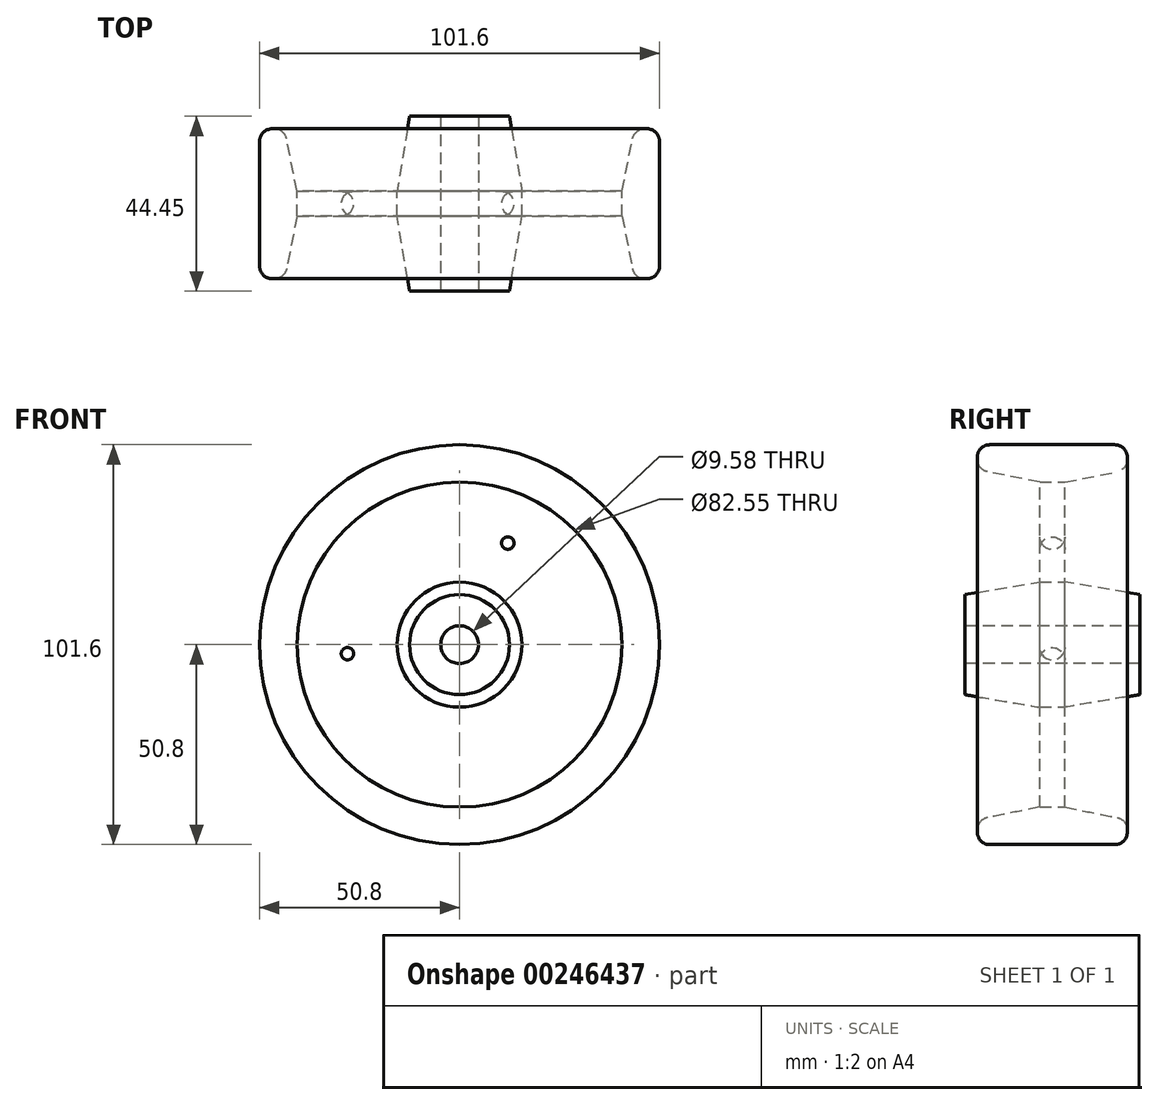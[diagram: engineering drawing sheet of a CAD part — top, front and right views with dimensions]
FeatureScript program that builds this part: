
annotation { "Feature Type Name" : "Feature", "Feature Type Description" : "" }
export const myFeature = defineFeature(function(context is Context, id is Id, definition is map)
    precondition{}
    {
        {
            var Q0;
            Q0=qCreatedBy(makeId("Right.planeOp"),FACE);
            var sketch = newSketch(context, id + "F0", { "sketchPlane" : qUnion([Q0])});
            skLineSegment(sketch, "E0", {"start": v(-6.26, 0) * mm, "end": v(19.14, 0) * mm});
            skLineSegment(sketch, "E1", {"start": v(-6.26, 4.79) * mm, "end": v(15.97, 4.79) * mm});
            skLineSegment(sketch, "E2", {"start": v(15.97, 4.79) * mm, "end": v(15.97, 50.8) * mm});
            skLineSegment(sketch, "E3", {"start": v(15.97, 50.8) * mm, "end": v(-3.08, 50.8) * mm});
            skLineSegment(sketch, "E4", {"start": v(-3.08, 50.8) * mm, "end": v(-3.08, 44.45) * mm});
            skLineSegment(sketch, "E5", {"start": v(-3.08, 44.45) * mm, "end": v(12.8, 41.28) * mm});
            skLineSegment(sketch, "E6", {"start": v(-6.26, 12.7) * mm, "end": v(12.8, 15.87) * mm});
            skLineSegment(sketch, "E7.trimOffspring", {"start": v(12.8, 15.87) * mm, "end": v(12.8, 41.28) * mm});
            skPoint(sketch, "E8.start.orphan", {"position": v(6.44, 0) * mm});
            skLineSegment(sketch, "E9.MirrorCS", {"start": v(35.02, 50.8) * mm, "end": v(35.02, 44.45) * mm});
            skLineSegment(sketch, "E10.MirrorCS", {"start": v(15.97, 50.8) * mm, "end": v(35.02, 50.8) * mm});
            skLineSegment(sketch, "E11.MirrorCS", {"start": v(35.02, 44.45) * mm, "end": v(19.14, 41.28) * mm});
            skLineSegment(sketch, "E12.MirrorCS", {"start": v(19.14, 15.88) * mm, "end": v(19.14, 41.28) * mm});
            skLineSegment(sketch, "E13.MirrorCS", {"start": v(38.2, 12.7) * mm, "end": v(19.14, 15.88) * mm});
            skLineSegment(sketch, "E14.MirrorCS", {"start": v(38.2, 0) * mm, "end": v(38.2, 12.7) * mm});
            skLineSegment(sketch, "E15.MirrorCS", {"start": v(38.2, 4.79) * mm, "end": v(15.97, 4.79) * mm});
            skLineSegment(sketch, "E16", {"start": v(-6.26, 12.7) * mm, "end": v(-6.26, 4.79) * mm});
            skSolve(sketch);
        }
        {
            var Q0;
            Q0=makeQuery(id+"F0.imprint","IMPRINT",FACE,{"disambiguationData":[TD([[makeQuery(id+"F0.imprint","IMPRINT",EDGE,{"derivedFrom":sQuery(id+"F0.wireOp",EDGE,"E2")}),-1.0]])]});
            var Q1;
            Q1=makeQuery(id+"F0.imprint","IMPRINT",FACE,{"disambiguationData":[TD([[makeQuery(id+"F0.imprint","IMPRINT",EDGE,{"derivedFrom":sQuery(id+"F0.wireOp",EDGE,"E1")}),1.0]])]});
            var Q2;
            Q2=sQuery(id+"F0.wireOp",EDGE,"E0");
            revolve(context, id + "F1", {"entities" : qUnion([Q0, Q1]), "axis" : qUnion([Q2]), "revolveType" : RevolveType.FULL});
        }
        {
            var Q0;
            Q0=makeQuery(id+"F1.opRevolve","SWEPT_FACE",FACE,{"disambiguationData":[OSD([sQuery(id+"F0.wireOp",EDGE,"E12.MirrorCS")])]});
            var sketch = newSketch(context, id + "F2", { "sketchPlane" : qUnion([Q0])});
            skCircle(sketch, "E17", {"center": v(0, 0) * mm, "radius": 28.58 * mm});
            skCircle(sketch, "E18", {"center": v(-12.26, 25.81) * mm, "radius": 4.76 * mm});
            skCircle(sketch, "E19.1.0", {"center": v(-16.23, -23.52) * mm, "radius": 4.76 * mm});
            skCircle(sketch, "E19.2.0", {"center": v(28.48, -2.3) * mm, "radius": 4.76 * mm});
            skSolve(sketch);
        }
        {
            var Q0;
            {var subQ0=sQuery(id+"F2.wireOp",EDGE,"E18");var subQ1=sQuery(id+"F2.wireOp",EDGE,"E17");var subQ2=makeQuery(id+"F2.imprint","INTERSECT",VERTEX,{"disambiguationData":[OD(0.0)],"derivedFrom":[subQ1,subQ0]});Q0=makeQuery(id+"F2.imprint","IMPRINT",FACE,{"disambiguationData":[TD([[makeQuery(id+"F2.imprint","IMPRINT",EDGE,{"disambiguationData":[TD([[subQ2,-1.0]])],"derivedFrom":subQ1}),1.0]])]});}
            var Q1;
            {var subQ0=sQuery(id+"F2.wireOp",EDGE,"E18");var subQ1=sQuery(id+"F2.wireOp",EDGE,"E17");var subQ2=makeQuery(id+"F2.imprint","INTERSECT",VERTEX,{"disambiguationData":[OD(0.0)],"derivedFrom":[subQ1,subQ0]});Q1=makeQuery(id+"F2.imprint","IMPRINT",FACE,{"disambiguationData":[TD([[makeQuery(id+"F2.imprint","IMPRINT",EDGE,{"disambiguationData":[TD([[subQ2,-1.0]])],"derivedFrom":subQ1}),-1.0]])]});}
            var Q2;
            {var subQ0=sQuery(id+"F2.wireOp",EDGE,"E19.2.0");var subQ1=sQuery(id+"F2.wireOp",EDGE,"E17");var subQ2=makeQuery(id+"F2.imprint","INTERSECT",VERTEX,{"disambiguationData":[OD(0.0)],"derivedFrom":[subQ1,subQ0]});Q2=makeQuery(id+"F2.imprint","IMPRINT",FACE,{"disambiguationData":[TD([[makeQuery(id+"F2.imprint","IMPRINT",EDGE,{"disambiguationData":[TD([[subQ2,1.0]])],"derivedFrom":subQ1}),1.0]])]});}
            var Q3;
            {var subQ0=sQuery(id+"F2.wireOp",EDGE,"E19.2.0");var subQ1=sQuery(id+"F2.wireOp",EDGE,"E17");var subQ2=makeQuery(id+"F2.imprint","INTERSECT",VERTEX,{"disambiguationData":[OD(0.0)],"derivedFrom":[subQ1,subQ0]});Q3=makeQuery(id+"F2.imprint","IMPRINT",FACE,{"disambiguationData":[TD([[makeQuery(id+"F2.imprint","IMPRINT",EDGE,{"disambiguationData":[TD([[subQ2,1.0]])],"derivedFrom":subQ1}),-1.0]])]});}
            var Q4;
            {var subQ0=sQuery(id+"F2.wireOp",EDGE,"E19.1.0");var subQ1=sQuery(id+"F2.wireOp",EDGE,"E17");var subQ2=makeQuery(id+"F2.imprint","INTERSECT",VERTEX,{"disambiguationData":[OD(0.0)],"derivedFrom":[subQ1,subQ0]});Q4=makeQuery(id+"F2.imprint","IMPRINT",FACE,{"disambiguationData":[TD([[makeQuery(id+"F2.imprint","IMPRINT",EDGE,{"disambiguationData":[TD([[subQ2,-1.0]])],"derivedFrom":subQ1}),-1.0]])]});}
            var Q5;
            {var subQ0=sQuery(id+"F2.wireOp",EDGE,"E19.1.0");var subQ1=sQuery(id+"F2.wireOp",EDGE,"E17");var subQ2=makeQuery(id+"F2.imprint","INTERSECT",VERTEX,{"disambiguationData":[OD(0.0)],"derivedFrom":[subQ1,subQ0]});Q5=makeQuery(id+"F2.imprint","IMPRINT",FACE,{"disambiguationData":[TD([[makeQuery(id+"F2.imprint","IMPRINT",EDGE,{"disambiguationData":[TD([[subQ2,-1.0]])],"derivedFrom":subQ1}),1.0]])]});}
            extrude(context, id + "F3", {"entities" : qUnion([Q0, Q1, Q2, Q3, Q4, Q5]), "operationType" : NewBodyOperationType.REMOVE, "oppositeDirection" : true, "depth" : 6.35 * mm});
        }
        {
            var Q0;
            Q0=makeQuery(id+"F1.opRevolve","SWEPT_FACE",FACE,{"disambiguationData":[OSD([sQuery(id+"F0.wireOp",EDGE,"E7.trimOffspring")])]});
            var Q1;
            Q1=makeQuery(id+"F1.opRevolve","SWEPT_FACE",FACE,{"disambiguationData":[OSD([sQuery(id+"F0.wireOp",EDGE,"E12.MirrorCS")])]});
            var Q2;
            Q2=makeQuery(id+"F1.opRevolve","SWEPT_FACE",FACE,{"disambiguationData":[OSD([sQuery(id+"F0.wireOp",EDGE,"E9.MirrorCS")])]});
            var Q3;
            Q3=makeQuery(id+"F1.opRevolve","SWEPT_FACE",FACE,{"disambiguationData":[OSD([sQuery(id+"F0.wireOp",EDGE,"E4")])]});
            fillet(context, id + "F4", {"entities" : qUnion([Q0, Q1, Q2, Q3]), "radius" : 3.17 * mm, "tangentPropagation" : true, "allowEdgeOverflow" : false});
        }
    });
